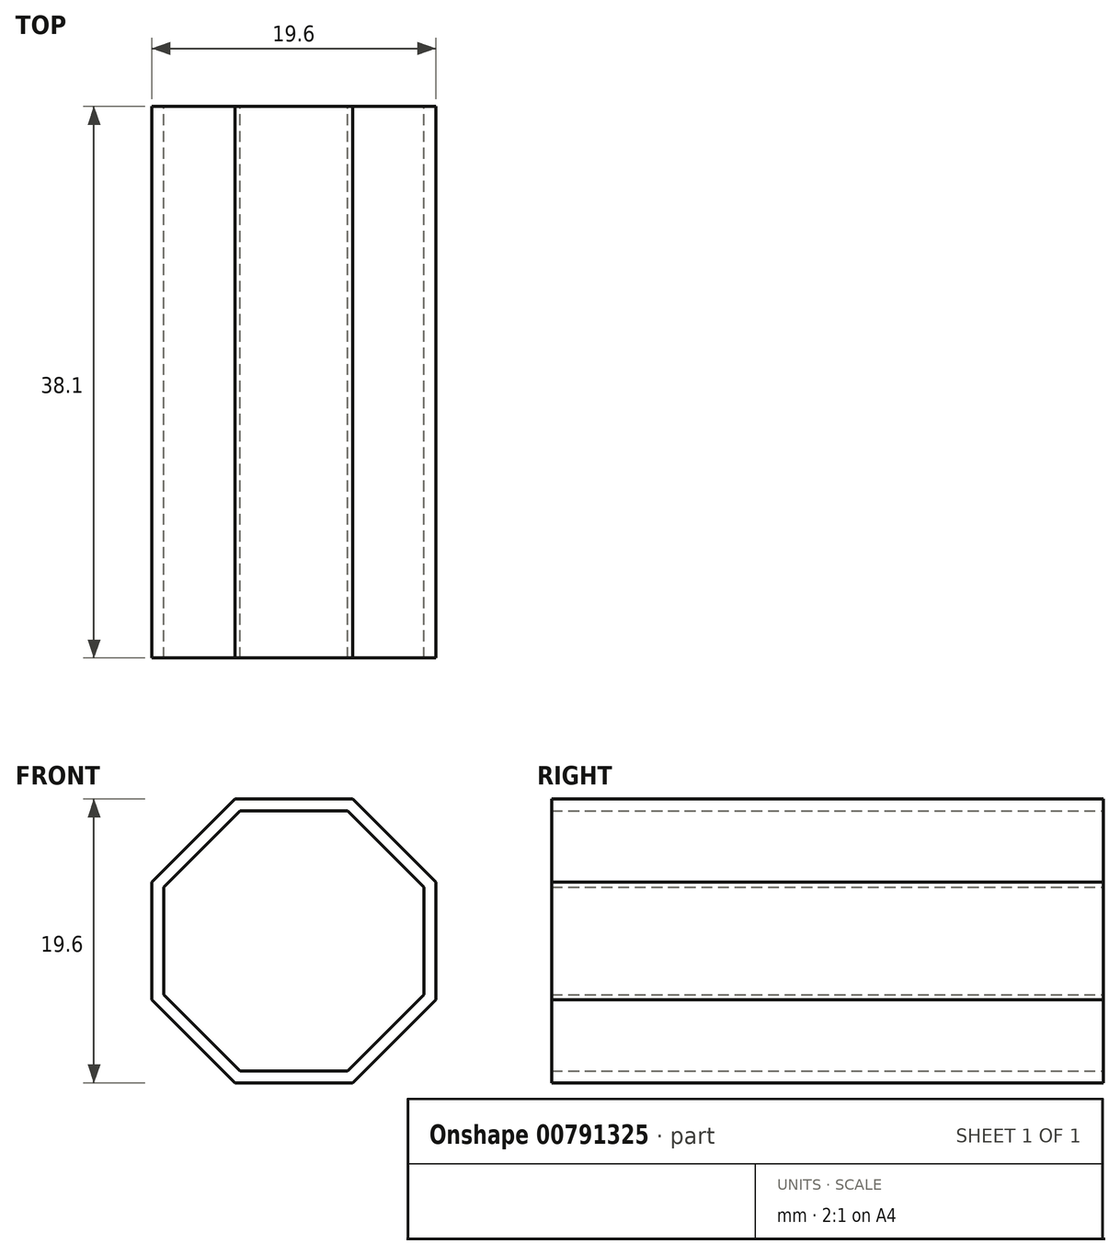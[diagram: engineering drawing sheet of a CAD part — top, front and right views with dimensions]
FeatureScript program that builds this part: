
annotation { "Feature Type Name" : "Feature", "Feature Type Description" : "" }
export const myFeature = defineFeature(function(context is Context, id is Id, definition is map)
    precondition{}
    {
        {
            var Q0;
            Q0=qCreatedBy(makeId("Front.planeOp"),FACE);
            var sketch = newSketch(context, id + "F0", { "sketchPlane" : qUnion([Q0])});
            skPoint(sketch, "E0", {"position": v(0, 9.8) * mm});
            skPoint(sketch, "E1", {"position": v(0, -9.8) * mm});
            skPoint(sketch, "E2", {"position": v(-9.8, 0) * mm});
            skPoint(sketch, "E3", {"position": v(9.8, 0) * mm});
            skLineSegment(sketch, "E4", {"start": v(0, 0) * mm, "end": v(-6.93, 6.93) * mm});
            skLineSegment(sketch, "E5", {"start": v(-6.93, -6.93) * mm, "end": v(0, 0) * mm});
            skLineSegment(sketch, "E6", {"start": v(6.93, 6.93) * mm, "end": v(0, 0) * mm});
            skLineSegment(sketch, "E7", {"start": v(6.93, -6.93) * mm, "end": v(0, 0) * mm});
            skLineSegment(sketch, "E8", {"start": v(0, 9.8) * mm, "end": v(0, 0) * mm, "construction": true});
            skPoint(sketch, "E9", {"position": v(-6.93, 6.93) * mm});
            skPoint(sketch, "E10", {"position": v(-6.93, -6.93) * mm});
            skPoint(sketch, "E11", {"position": v(6.93, -6.93) * mm});
            skPoint(sketch, "E12", {"position": v(6.93, 6.93) * mm});
            skLineSegment(sketch, "E13", {"start": v(9.8, 4.06) * mm, "end": v(9.8, -4.06) * mm});
            skLineSegment(sketch, "E14", {"start": v(-4.06, -9.8) * mm, "end": v(4.06, -9.8) * mm});
            skLineSegment(sketch, "E15", {"start": v(-9.8, 4.06) * mm, "end": v(-4.06, 9.8) * mm});
            skLineSegment(sketch, "E16", {"start": v(4.06, 9.8) * mm, "end": v(9.8, 4.06) * mm});
            skLineSegment(sketch, "E17", {"start": v(9.8, -4.06) * mm, "end": v(4.06, -9.8) * mm});
            skLineSegment(sketch, "E18", {"start": v(-9.8, -4.06) * mm, "end": v(-4.06, -9.8) * mm});
            skLineSegment(sketch, "E19.trimOffspring", {"start": v(-4.06, 9.8) * mm, "end": v(4.06, 9.8) * mm});
            skLineSegment(sketch, "E20.trimOffspring", {"start": v(-9.8, 4.06) * mm, "end": v(-9.8, -4.06) * mm});
            skPoint(sketch, "E21.start.orphan", {"position": v(-10.63, 9.8) * mm});
            skPoint(sketch, "E22.start.orphan", {"position": v(-9.8, 11.44) * mm});
            skPoint(sketch, "E23.orphan", {"position": v(-10.58, -9.8) * mm});
            skPoint(sketch, "E24.orphan", {"position": v(9.8, 12.1) * mm});
            skPoint(sketch, "E25.orphan", {"position": v(13.86, 0) * mm});
            skPoint(sketch, "E26", {"position": v(0, 0) * mm});
            skPoint(sketch, "E27", {"position": v(-9.8, 4.06) * mm});
            skPoint(sketch, "E28", {"position": v(-4.06, 9.8) * mm});
            skPoint(sketch, "E29", {"position": v(4.06, 9.8) * mm});
            skPoint(sketch, "E30", {"position": v(9.8, 4.06) * mm});
            skPoint(sketch, "E31", {"position": v(9.8, -4.06) * mm});
            skPoint(sketch, "E32", {"position": v(4.06, -9.8) * mm});
            skPoint(sketch, "E33", {"position": v(-4.06, -9.8) * mm});
            skPoint(sketch, "E34", {"position": v(-9.8, -4.06) * mm});
            skLineSegment(sketch, "E35", {"start": v(0, 0) * mm, "end": v(4.06, 9.8) * mm, "construction": true});
            skLineSegment(sketch, "E36", {"start": v(0, 0) * mm, "end": v(9.8, 4.06) * mm, "construction": true});
            skLineSegment(sketch, "E37", {"start": v(0, 0) * mm, "end": v(9.8, -4.06) * mm, "construction": true});
            skLineSegment(sketch, "E38", {"start": v(0, 0) * mm, "end": v(4.06, -9.8) * mm, "construction": true});
            skLineSegment(sketch, "E39", {"start": v(0, 0) * mm, "end": v(0, -9.8) * mm, "construction": true});
            skLineSegment(sketch, "E40.MirrorCS", {"start": v(0, 0) * mm, "end": v(-4.06, 9.8) * mm, "construction": true});
            skLineSegment(sketch, "E41.MirrorCS", {"start": v(0, 0) * mm, "end": v(-9.8, 4.06) * mm, "construction": true});
            skLineSegment(sketch, "E42.MirrorCS", {"start": v(0, 0) * mm, "end": v(-9.8, -4.06) * mm, "construction": true});
            skLineSegment(sketch, "E43.MirrorCS", {"start": v(0, 0) * mm, "end": v(-4.06, -9.8) * mm, "construction": true});
            skPoint(sketch, "E44", {"position": v(-8.98, 3.72) * mm});
            skLineSegment(sketch, "E45", {"start": v(-8.98, 3.72) * mm, "end": v(-8.98, -3.72) * mm});
            skLineSegment(sketch, "E46", {"start": v(-8.98, -3.72) * mm, "end": v(-3.72, -8.98) * mm});
            skLineSegment(sketch, "E47", {"start": v(-3.72, -8.98) * mm, "end": v(3.72, -8.98) * mm});
            skLineSegment(sketch, "E48", {"start": v(3.72, -8.98) * mm, "end": v(8.98, -3.72) * mm});
            skLineSegment(sketch, "E49", {"start": v(8.98, -3.72) * mm, "end": v(8.98, 3.72) * mm});
            skLineSegment(sketch, "E50", {"start": v(8.98, 3.72) * mm, "end": v(3.72, 8.98) * mm});
            skLineSegment(sketch, "E51", {"start": v(3.72, 8.98) * mm, "end": v(-3.72, 8.98) * mm});
            skLineSegment(sketch, "E52", {"start": v(-3.72, 8.98) * mm, "end": v(-8.98, 3.72) * mm});
            skSolve(sketch);
        }
        {
            var Q0;
            {var subQ3=sQuery(id+"F0.wireOp",EDGE,"E19.trimOffspring");Q0=makeQuery(id+"F0.imprint","IMPRINT",FACE,{"disambiguationData":[TD([[makeQuery(id+"F0.imprint","IMPRINT",EDGE,{"derivedFrom":subQ3}),-1.0]])]});}
            var Q1;
            {var subQ3=sQuery(id+"F0.wireOp",EDGE,"E20.trimOffspring");Q1=makeQuery(id+"F0.imprint","IMPRINT",FACE,{"disambiguationData":[TD([[makeQuery(id+"F0.imprint","IMPRINT",EDGE,{"derivedFrom":subQ3}),1.0]])]});}
            var Q2;
            {var subQ3=sQuery(id+"F0.wireOp",EDGE,"E13");Q2=makeQuery(id+"F0.imprint","IMPRINT",FACE,{"disambiguationData":[TD([[makeQuery(id+"F0.imprint","IMPRINT",EDGE,{"derivedFrom":subQ3}),-1.0]])]});}
            var Q3;
            {var subQ3=sQuery(id+"F0.wireOp",EDGE,"E14");Q3=makeQuery(id+"F0.imprint","IMPRINT",FACE,{"disambiguationData":[TD([[makeQuery(id+"F0.imprint","IMPRINT",EDGE,{"derivedFrom":subQ3}),1.0]])]});}
            extrude(context, id + "F1", {"entities" : qUnion([Q0, Q1, Q2, Q3]), "endBound" : BoundingType.SYMMETRIC, "depth" : 38.1 * mm, "offsetDistance" : 25.4 * mm});
        }
    });
